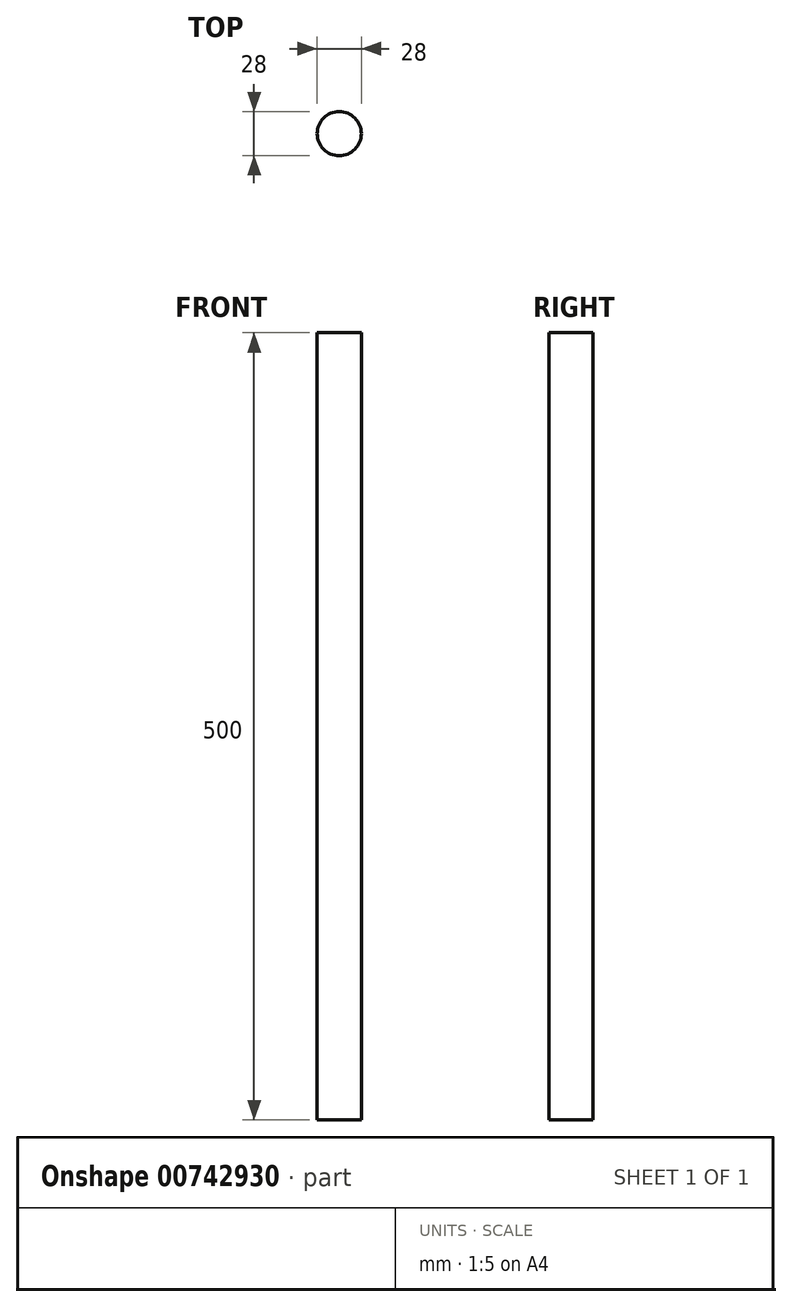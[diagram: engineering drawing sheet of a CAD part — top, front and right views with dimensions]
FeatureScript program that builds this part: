
annotation { "Feature Type Name" : "Feature", "Feature Type Description" : "" }
export const myFeature = defineFeature(function(context is Context, id is Id, definition is map)
    precondition{}
    {
        {
            var Q0;
            Q0=qCreatedBy(makeId("Top.planeOp"),FACE);
            var sketch = newSketch(context, id + "F0", { "sketchPlane" : qUnion([Q0])});
            skCircle(sketch, "E0", {"center": v(0, 0) * mm, "radius": 14 * mm});
            skSolve(sketch);
        }
        {
            var Q0;
            Q0 = qSketchRegion(id + "F0", true);
            extrude(context, id + "F1", {"entities" : qUnion([Q0]), "depth" : 500 * mm, "offsetDistance" : 25 * mm});
        }
    });
